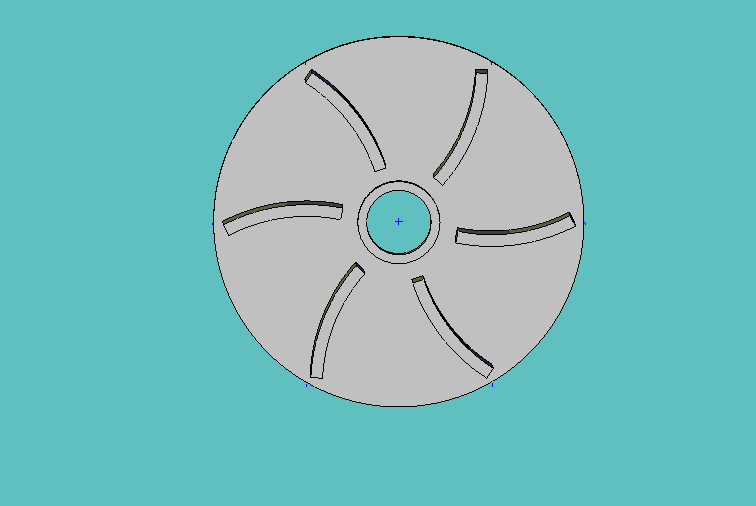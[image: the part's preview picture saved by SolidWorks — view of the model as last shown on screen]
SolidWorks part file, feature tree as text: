
SOLIDWORKS PART (.sldprt)
format: sldprt  version: not decoded by parser v0  size: 1,036,288 bytes
history: native  units: mm
features: sketch x7, pattern_circular x7, extrude x4, material x1, hole x1 (+12 scaffold rows collapsed)
feature tree (32):
  scaffold x12  (default folders/planes/origin — collapsed)
  material  "Material <not specified>"
  sketch  "Sketch1"  dims[D1=63.0mm]
  extrude  "Extrude1"  Depth=4mm
  sketch  "Sketch2"  dims[c1.D1=20.0mm c1.D2=70.0mm c1.D3=40.0mm c1.D4=20.0mm c2.D3=20.0mm c2.D2=70.0mm c2.D4=12.0mm c2.D5=12.0mm c2.D6=8.0mm c3.D5=35.0mm c3.D2=2.0mm c3.D1=13.0mm c4.D5=2.0mm c4.D6=1.0mm c4.D7=5.0mm]
  pattern_circular  "CirPattern1"  Count=4 Angle=360deg
  pattern_circular  "CirPattern2"  Count=5 Angle=360deg
  extrude  "Extrude-Thin2"  [1 undecoded]
  sketch  "Sketch2<5>"  dims[D1=10.0mm D5=2.0mm D6=1.0mm D7=5.0mm]
  pattern_circular  "CirPattern3"  Count=4 Angle=360deg
  pattern_circular  "CirPattern4"  Count=5 Angle=360deg
  extrude  "Extrude-Thin3"  [1 undecoded]
  sketch  "Sketch2<6>"  dims[D1=10.0mm D5=2.0mm D6=1.0mm D7=5.0mm]
  pattern_circular  "CirPattern5"  Count=4 Angle=360deg
  pattern_circular  "CirPattern6"  Count=5 Angle=360deg
  pattern_circular  "CirPattern7"  Count=6 Angle=360deg
  sketch  "Sketch3"  dims[D1=14.0mm]
  extrude  "Extrude2"  Depth=10mm
  hole  "M11.0 (11) Diameter Hole1"  Diameter=11mm Depth=10mm
  sketch  "Sketch5"
  sketch  "Sketch4"  dims[hole-wizard template sketch: 47 standard entries collapsed; hole parameters kept: c15.Hole Depth=10.0mm c15.D3=~14.816244mm c15.Drill Angle=118.0deg]
decode coverage: 16 of 19 modeling features carry decoded parameters
note: ~ marks probable driven/reference dimensions
note: 2 parameter values undecoded
note: suppression state not decoded; provenance and decode notes live in map.json
